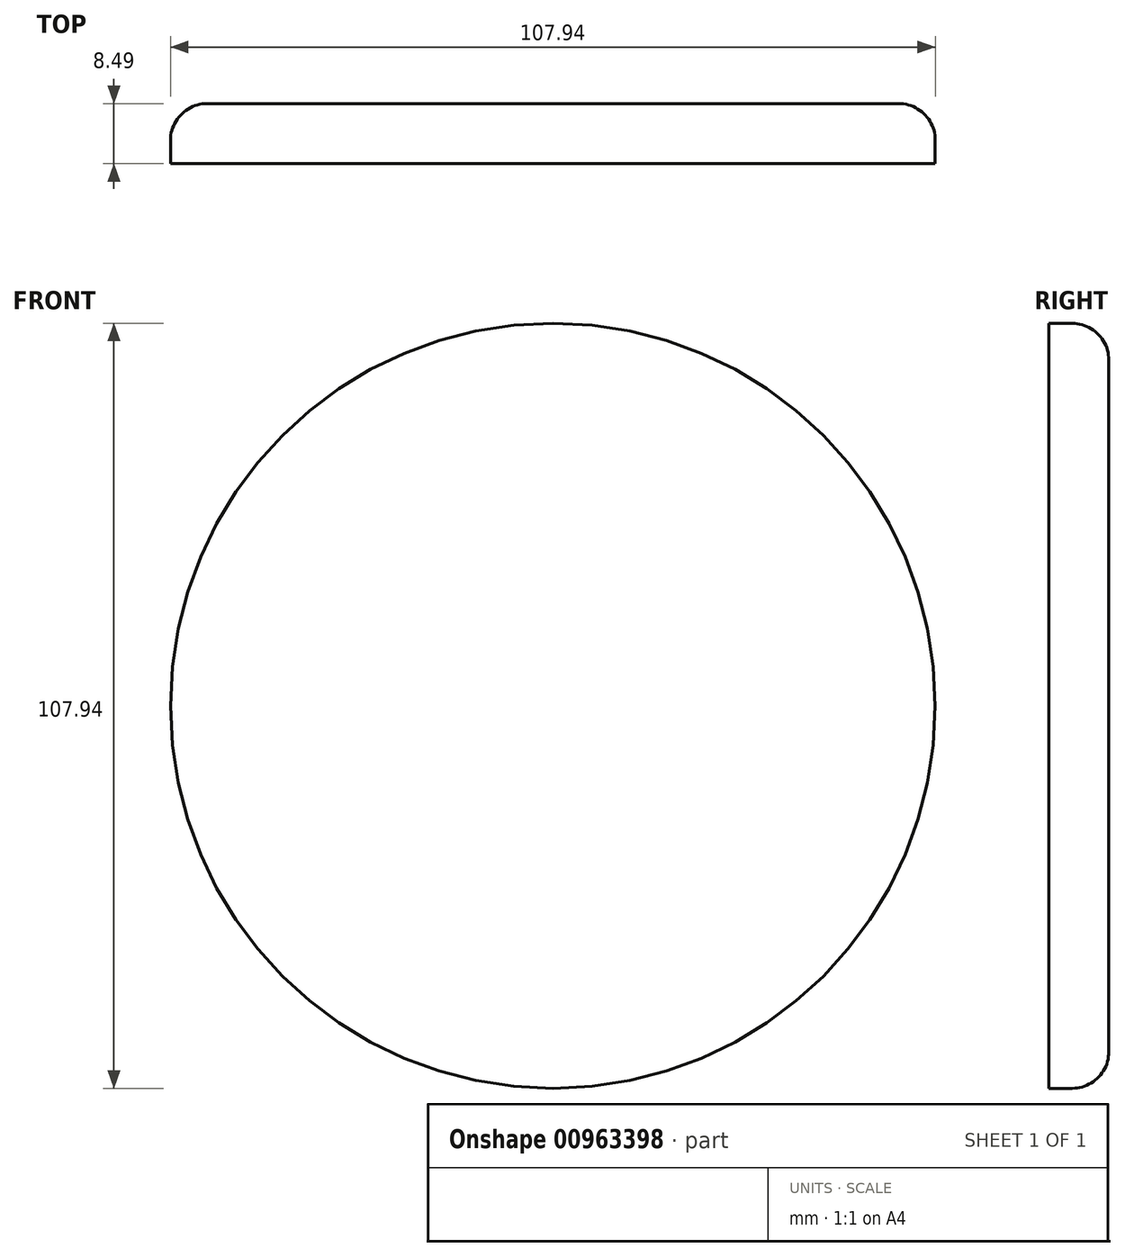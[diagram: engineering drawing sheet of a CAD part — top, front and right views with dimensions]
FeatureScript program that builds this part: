
annotation { "Feature Type Name" : "Feature", "Feature Type Description" : "" }
export const myFeature = defineFeature(function(context is Context, id is Id, definition is map)
    precondition{}
    {
        {
            var Q0;
            Q0=qCreatedBy(makeId("Front.planeOp"),FACE);
            var sketch = newSketch(context, id + "F0", { "sketchPlane" : qUnion([Q0])});
            skCircle(sketch, "E0", {"center": v(0, 0) * mm, "radius": 53.97 * mm});
            skSolve(sketch);
        }
        {
            var Q0;
            Q0=makeQuery(id+"F0.imprint","IMPRINT",FACE,{"disambiguationData":[TD([[makeQuery(id+"F0.imprint","IMPRINT",EDGE,{"derivedFrom":sQuery(id+"F0.wireOp",EDGE,"E0")}),1.0]])]});
            extrude(context, id + "F1", {"entities" : qUnion([Q0]), "depth" : 8.5 * mm, "offsetDistance" : 25.4 * mm});
        }
        {
            var Q0;
            Q0=makeQuery(id+"F1.opExtrude","CAP_EDGE",EDGE,{"disambiguationData":[OSD([sQuery(id+"F0.wireOp",EDGE,"E0")])],"isStart":true});
            fillet(context, id + "F2", {"entities" : qUnion([Q0]), "tangentPropagation" : true, "radius" : 5.16 * mm, "defaultsChanged" : true, "vertexSettings" : [], "allowEdgeOverflow" : false});
        }
    });
